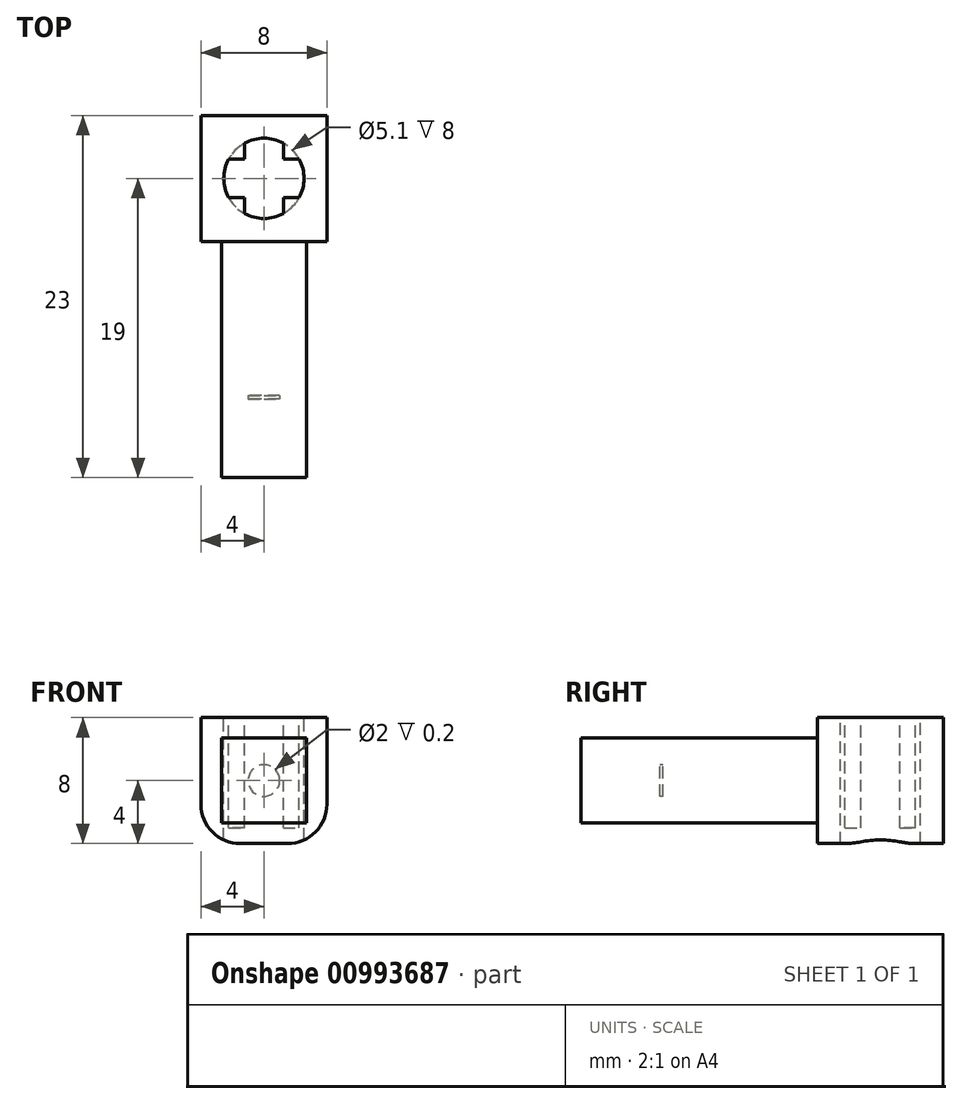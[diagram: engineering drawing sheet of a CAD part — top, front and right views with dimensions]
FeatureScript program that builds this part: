
annotation { "Feature Type Name" : "Feature", "Feature Type Description" : "" }
export const myFeature = defineFeature(function(context is Context, id is Id, definition is map)
    precondition{}
    {
        {
            var Q0;
            Q0=qCreatedBy(makeId("Front.planeOp"),FACE);
            var sketch = newSketch(context, id + "F0", { "sketchPlane" : qUnion([Q0])});
            skCircle(sketch, "E0", {"center": v(0, 0) * mm, "radius": 2.6 * mm});
            skSolve(sketch);
        }
        {
            var Q0;
            Q0=makeQuery(id+"F0.imprint","IMPRINT",FACE,{"disambiguationData":[TD([[makeQuery(id+"F0.imprint","IMPRINT",EDGE,{"derivedFrom":sQuery(id+"F0.wireOp",EDGE,"E0")}),1.0]])]});
            extrude(context, id + "F1", {"entities" : qUnion([Q0]), "depth" : 10 * mm});
        }
        {
            var Q0;
            Q0=makeQuery(id+"F1.opExtrude","CAP_FACE",FACE,{"disambiguationData":[OSD([sQuery(id+"F0.wireOp",EDGE,"E0")])],"isStart":true});
            var sketch = newSketch(context, id + "F2", { "sketchPlane" : qUnion([Q0])});
            skLineSegment(sketch, "E1.bottom", {"start": v(-4, 4) * mm, "end": v(4, 4) * mm});
            skLineSegment(sketch, "E1.top", {"start": v(-1.5, -4) * mm, "end": v(1.5, -4) * mm});
            skLineSegment(sketch, "E1.left", {"start": v(-4, 4) * mm, "end": v(-4, -1.5) * mm});
            skLineSegment(sketch, "E1.right", {"start": v(4, 4) * mm, "end": v(4, -1.5) * mm});
            skPoint(sketch, "E1.middle", {"position": v(0, 0) * mm});
            skPoint(sketch, "E2.visualSharp", {"position": v(-4, -4) * mm});
            skArc(sketch, "E2.filletArc", {"start": v(-4, -1.5) * mm, "mid": v(-3.27, -3.27) * mm, "end": v(-1.5, -4) * mm});
            skPoint(sketch, "E3.visualSharp", {"position": v(4, -4) * mm});
            skArc(sketch, "E3.filletArc", {"start": v(1.5, -4) * mm, "mid": v(3.27, -3.27) * mm, "end": v(4, -1.5) * mm});
            skSolve(sketch);
        }
        {
            var Q0;
            Q0=makeQuery(id+"F2.imprint","IMPRINT",FACE,{"disambiguationData":[TD([[makeQuery(id+"F2.imprint","IMPRINT",EDGE,{"derivedFrom":sQuery(id+"F2.wireOp",EDGE,"E1.bottom")}),-1.0]])]});
            var Q1;
            Q1=makeQuery(id+"F2.imprint","IMPRINT",FACE,{"disambiguationData":[TD([[makeQuery(id+"F2.imprint","IMPRINT",EDGE,{"derivedFrom":makeQuery(id+"F1.opExtrude","CAP_EDGE",EDGE,{"disambiguationData":[OSD([sQuery(id+"F0.wireOp",EDGE,"E0")])],"isStart":true})}),-1.0]])]});
            extrude(context, id + "F3", {"entities" : qUnion([Q0, Q1]), "operationType" : NewBodyOperationType.ADD, "depth" : 8 * mm});
        }
        {
            var Q0;
            Q0=makeQuery(id+"F3.opExtrude","SWEPT_FACE",FACE,{"disambiguationData":[OSD([sQuery(id+"F2.wireOp",EDGE,"E1.bottom")])]});
            var sketch = newSketch(context, id + "F4", { "sketchPlane" : qUnion([Q0])});
            skCircle(sketch, "E4", {"center": v(0, 4) * mm, "radius": 2.55 * mm});
            skSolve(sketch);
        }
        {
            var Q0;
            Q0=makeQuery(id+"F4.imprint","IMPRINT",FACE,{"disambiguationData":[TD([[makeQuery(id+"F4.imprint","IMPRINT",EDGE,{"derivedFrom":sQuery(id+"F4.wireOp",EDGE,"E4")}),1.0]])]});
            extrude(context, id + "F5", {"entities" : qUnion([Q0]), "operationType" : NewBodyOperationType.REMOVE, "endBound" : BoundingType.THROUGH_ALL, "oppositeDirection" : true, "depth" : 25 * mm});
        }
        {
            var Q0;
            Q0=makeQuery(id+"F1.opExtrude","CAP_FACE",FACE,{"disambiguationData":[OSD([sQuery(id+"F0.wireOp",EDGE,"E0")])],"isStart":false});
            var sketch = newSketch(context, id + "F6", { "sketchPlane" : qUnion([Q0])});
            skCircle(sketch, "E5", {"center": v(0, 0) * mm, "radius": 1 * mm});
            skSolve(sketch);
        }
        {
            var Q0;
            Q0=makeQuery(id+"F6.imprint","IMPRINT",FACE,{"disambiguationData":[TD([[makeQuery(id+"F6.imprint","IMPRINT",EDGE,{"derivedFrom":sQuery(id+"F6.wireOp",EDGE,"E5")}),1.0]])]});
            extrude(context, id + "F7", {"entities" : qUnion([Q0]), "operationType" : NewBodyOperationType.REMOVE, "oppositeDirection" : true, "depth" : 0.2 * mm});
        }
        {
            var Q0;
            Q0=makeQuery(id+"F3.opExtrude","CAP_FACE",FACE,{"disambiguationData":[OSD([sQuery(id+"F2.wireOp",EDGE,"E1.bottom"),sQuery(id+"F2.wireOp",EDGE,"E1.top"),sQuery(id+"F2.wireOp",EDGE,"E1.left"),sQuery(id+"F2.wireOp",EDGE,"E1.right")])],"isStart":true});
            var sketch = newSketch(context, id + "F8", { "sketchPlane" : qUnion([Q0])});
            skLineSegment(sketch, "E6.bottom", {"start": v(-2.7, 2.7) * mm, "end": v(2.7, 2.7) * mm});
            skLineSegment(sketch, "E6.top", {"start": v(-2.7, -2.7) * mm, "end": v(2.7, -2.7) * mm});
            skLineSegment(sketch, "E6.left", {"start": v(-2.7, 2.7) * mm, "end": v(-2.7, -2.7) * mm});
            skLineSegment(sketch, "E6.right", {"start": v(2.7, 2.7) * mm, "end": v(2.7, -2.7) * mm});
            skPoint(sketch, "E6.middle", {"position": v(0, 0) * mm});
            skSolve(sketch);
        }
        {
            var Q0;
            Q0=makeQuery(id+"F8.imprint","IMPRINT",FACE,{"disambiguationData":[TD([[makeQuery(id+"F8.imprint","IMPRINT",EDGE,{"derivedFrom":sQuery(id+"F8.wireOp",EDGE,"E6.bottom")}),-1.0]])]});
            extrude(context, id + "F9", {"entities" : qUnion([Q0]), "operationType" : NewBodyOperationType.ADD, "depth" : 15 * mm});
        }
        {
            var Q0;
            Q0=makeQuery(id+"F3.opExtrude","SWEPT_FACE",FACE,{"disambiguationData":[OSD([sQuery(id+"F2.wireOp",EDGE,"E1.bottom")])]});
            var sketch = newSketch(context, id + "F10", { "sketchPlane" : qUnion([Q0])});
            skLineSegment(sketch, "E7", {"start": v(-1.23, 5.23) * mm, "end": v(-1.23, 6.23) * mm});
            skLineSegment(sketch, "E8", {"start": v(-1.23, 5.23) * mm, "end": v(-2.23, 5.23) * mm});
            skArc(sketch, "E9", {"start": v(-2.23, 5.23) * mm, "mid": v(2.04, 2.47) * mm, "end": v(-1.8, 5.8) * mm});
            skSolve(sketch);
        }
        {
            var Q0;
            {var subQ0=sQuery(id+"F10.wireOp",EDGE,"E7");Q0=makeQuery(id+"F10.imprint","IMPRINT",FACE,{"disambiguationData":[TD([[makeQuery(id+"F10.imprint","IMPRINT",EDGE,{"derivedFrom":subQ0}),1.0]])]});}
            extrude(context, id + "F11", {"entities" : qUnion([Q0]), "operationType" : NewBodyOperationType.ADD, "oppositeDirection" : true, "depth" : 7 * mm});
        }
        {
            var Q0;
            Q0=makeQuery(id+"F11.boolean.opBoolean","MERGE",FACE,{"derivedFrom":[makeQuery(id+"F3.opExtrude","SWEPT_FACE",FACE,{"disambiguationData":[OSD([sQuery(id+"F2.wireOp",EDGE,"E1.bottom")])]}),makeQuery(id+"F11.opExtrude","CAP_FACE",FACE,{"disambiguationData":[OSD([sQuery(id+"F4.wireOp",EDGE,"E4"),sQuery(id+"F10.wireOp",EDGE,"E7"),sQuery(id+"F10.wireOp",EDGE,"E8"),sQuery(id+"F10.wireOp",EDGE,"E9")])],"isStart":true})]});
            var sketch = newSketch(context, id + "F12", { "sketchPlane" : qUnion([Q0])});
            skLineSegment(sketch, "E10", {"start": v(1.23, 6.23) * mm, "end": v(1.23, 5.23) * mm});
            skLineSegment(sketch, "E11", {"start": v(1.23, 5.23) * mm, "end": v(2.23, 5.23) * mm});
            skSolve(sketch);
        }
        {
            var Q0;
            {var subQ0=sQuery(id+"F12.wireOp",EDGE,"E10");Q0=makeQuery(id+"F12.imprint","IMPRINT",FACE,{"disambiguationData":[TD([[makeQuery(id+"F12.imprint","IMPRINT",EDGE,{"derivedFrom":subQ0}),1.0]])]});}
            extrude(context, id + "F13", {"entities" : qUnion([Q0]), "operationType" : NewBodyOperationType.ADD, "oppositeDirection" : true, "depth" : 7 * mm});
        }
        {
            var Q0;
            {var subQ0=sQuery(id+"F4.wireOp",EDGE,"E4");Q0=makeQuery(id+"F13.boolean.opBoolean","MERGE",FACE,{"derivedFrom":[makeQuery(id+"F11.boolean.opBoolean","MERGE",FACE,{"derivedFrom":[makeQuery(id+"F3.opExtrude","SWEPT_FACE",FACE,{"disambiguationData":[OSD([sQuery(id+"F2.wireOp",EDGE,"E1.bottom")])]}),makeQuery(id+"F11.opExtrude","CAP_FACE",FACE,{"disambiguationData":[OSD([subQ0,sQuery(id+"F10.wireOp",EDGE,"E7"),sQuery(id+"F10.wireOp",EDGE,"E8"),sQuery(id+"F10.wireOp",EDGE,"E9")])],"isStart":true})]}),makeQuery(id+"F13.opExtrude","CAP_FACE",FACE,{"disambiguationData":[OSD([subQ0,sQuery(id+"F12.wireOp",EDGE,"E10"),sQuery(id+"F12.wireOp",EDGE,"E11")])],"isStart":true})]});}
            var sketch = newSketch(context, id + "F14", { "sketchPlane" : qUnion([Q0])});
            skLineSegment(sketch, "E12", {"start": v(-1.23, 1.77) * mm, "end": v(-1.23, 2.77) * mm});
            skLineSegment(sketch, "E13", {"start": v(-1.23, 2.77) * mm, "end": v(-2.23, 2.77) * mm});
            skLineSegment(sketch, "E14.MirrorCS", {"start": v(1.23, 2.77) * mm, "end": v(2.23, 2.77) * mm});
            skLineSegment(sketch, "E15.MirrorCS", {"start": v(1.23, 1.77) * mm, "end": v(1.23, 2.77) * mm});
            skSolve(sketch);
        }
        {
            var Q0;
            {var subQ0=sQuery(id+"F14.wireOp",EDGE,"E12");Q0=makeQuery(id+"F14.imprint","IMPRINT",FACE,{"disambiguationData":[TD([[makeQuery(id+"F14.imprint","IMPRINT",EDGE,{"derivedFrom":subQ0}),1.0]])]});}
            extrude(context, id + "F15", {"entities" : qUnion([Q0]), "operationType" : NewBodyOperationType.ADD, "oppositeDirection" : true, "depth" : 7 * mm});
        }
        {
            var Q0;
            {var subQ0=sQuery(id+"F14.wireOp",EDGE,"E14.MirrorCS");Q0=makeQuery(id+"F14.imprint","IMPRINT",FACE,{"disambiguationData":[TD([[makeQuery(id+"F14.imprint","IMPRINT",EDGE,{"derivedFrom":subQ0}),-1.0]])]});}
            extrude(context, id + "F16", {"entities" : qUnion([Q0]), "operationType" : NewBodyOperationType.ADD, "oppositeDirection" : true, "depth" : 7 * mm});
        }
        {
            var Q0;
            Q0=makeQuery(id+"F6.imprint","IMPRINT",FACE,{"disambiguationData":[TD([[makeQuery(id+"F6.imprint","IMPRINT",EDGE,{"derivedFrom":sQuery(id+"F6.wireOp",EDGE,"E5")}),-1.0]])]});
            var Q1;
            Q1=makeQuery(id+"F6.imprint","IMPRINT",FACE,{"disambiguationData":[TD([[makeQuery(id+"F6.imprint","IMPRINT",EDGE,{"derivedFrom":sQuery(id+"F6.wireOp",EDGE,"E5")}),1.0]])]});
            extrude(context, id + "F17", {"entities" : qUnion([Q0, Q1]), "operationType" : NewBodyOperationType.ADD, "depth" : 5 * mm});
        }
    });
